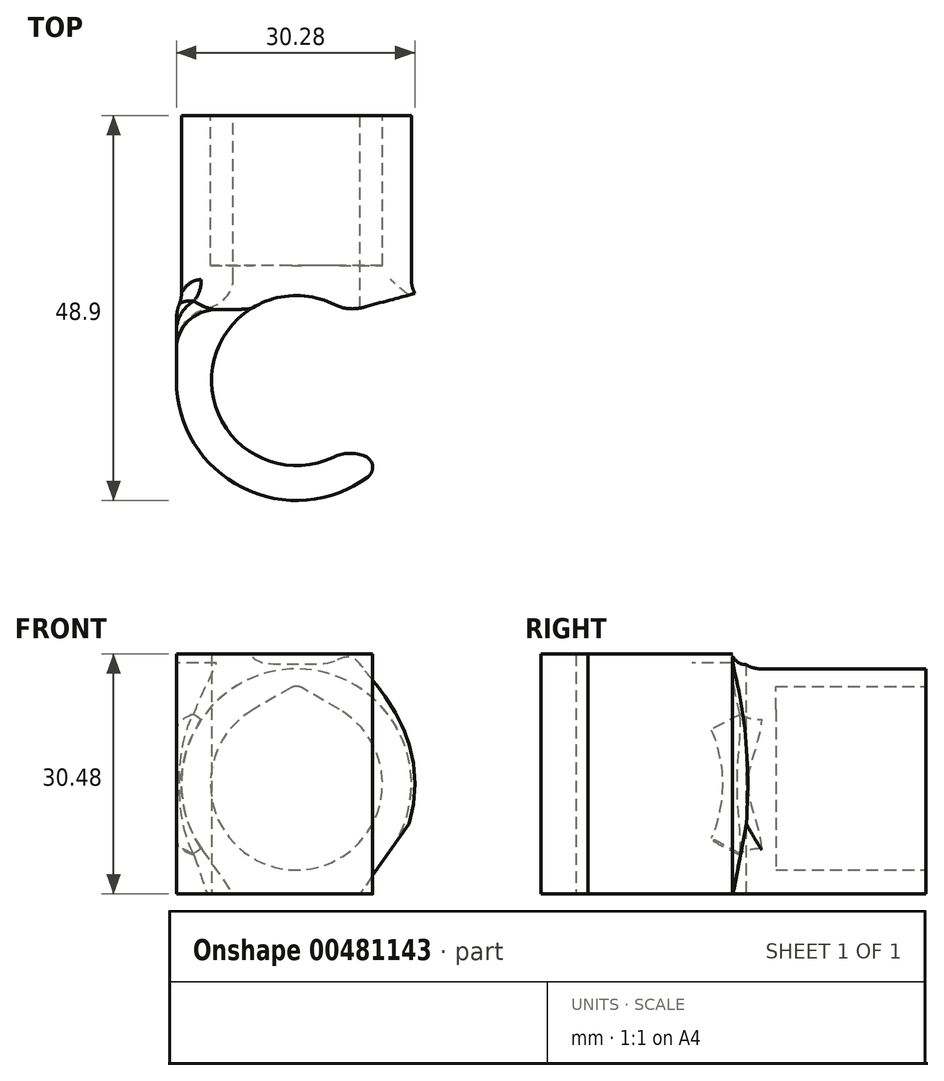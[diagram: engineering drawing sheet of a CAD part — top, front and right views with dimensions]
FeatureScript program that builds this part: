
annotation { "Feature Type Name" : "Feature", "Feature Type Description" : "" }
export const myFeature = defineFeature(function(context is Context, id is Id, definition is map)
    precondition{}
    {
        {
            var Q0;
            Q0=qCreatedBy(makeId("Top.planeOp"),FACE);
            var sketch = newSketch(context, id + "F0", { "sketchPlane" : qUnion([Q0])});
            skArc(sketch, "E0", {"start": v(4.84, 9.65) * mm, "mid": v(-10.8, 0.11) * mm, "end": v(4.64, -9.75) * mm});
            skArc(sketch, "E1", {"start": v(-15.24, 0) * mm, "mid": v(-6.85, -13.61) * mm, "end": v(9.08, -12.24) * mm});
            skLineSegment(sketch, "E2", {"start": v(-15.24, 0) * mm, "end": v(-15.24, 33.66) * mm});
            skLineSegment(sketch, "E3", {"start": v(15.24, 11.11) * mm, "end": v(15.24, 33.66) * mm});
            skLineSegment(sketch, "E4", {"start": v(15.24, 33.66) * mm, "end": v(-15.24, 33.66) * mm});
            skPoint(sketch, "E5.orphan", {"position": v(-10.8, 0) * mm});
            skPoint(sketch, "E6.start.orphan", {"position": v(10.8, 0) * mm});
            skLineSegment(sketch, "E7", {"start": v(8.43, 9.29) * mm, "end": v(15.24, 11.11) * mm});
            skPoint(sketch, "E8.orphan", {"position": v(15.24, 0) * mm});
            skPoint(sketch, "E9.visualSharp", {"position": v(6.35, 8.73) * mm});
            skArc(sketch, "E9.filletArc", {"start": v(4.84, 9.65) * mm, "mid": v(6.6, 9.14) * mm, "end": v(8.43, 9.29) * mm});
            skPoint(sketch, "E10.visualSharp", {"position": v(6.1, -8.9) * mm});
            skArc(sketch, "E10.filletArc", {"start": v(8.76, -9.64) * mm, "mid": v(6.69, -9.26) * mm, "end": v(4.64, -9.75) * mm});
            skArc(sketch, "E11", {"start": v(8.76, -9.64) * mm, "mid": v(9.68, -10.85) * mm, "end": v(9.08, -12.24) * mm});
            skSolve(sketch);
        }
        {
            var Q0;
            Q0 = qSketchRegion(id + "F0", true);
            extrude(context, id + "F1", {"entities" : qUnion([Q0]), "depth" : 30.48 * mm});
        }
        {
            var Q0;
            Q0=makeQuery(id+"F1.opExtrude","SWEPT_FACE",FACE,{"disambiguationData":[OSD([sQuery(id+"F0.wireOp",EDGE,"E4")])]});
            var sketch = newSketch(context, id + "F2", { "sketchPlane" : qUnion([Q0])});
            skArc(sketch, "E12", {"start": v(-5.46, 23.43) * mm, "mid": v(0, 3.05) * mm, "end": v(5.46, 23.43) * mm});
            skLineSegment(sketch, "E13", {"start": v(-5.46, 23.43) * mm, "end": v(-0.64, 26.22) * mm});
            skLineSegment(sketch, "E14", {"start": v(0.64, 26.22) * mm, "end": v(5.46, 23.43) * mm});
            skPoint(sketch, "E15.visualSharp", {"position": v(0, 26.58) * mm});
            skArc(sketch, "E15.filletArc", {"start": v(0.63, 26.22) * mm, "mid": v(0, 26.39) * mm, "end": v(-0.64, 26.22) * mm});
            skSolve(sketch);
        }
        {
            var Q0;
            Q0 = qSketchRegion(id + "F2", true);
            extrude(context, id + "F3", {"entities" : qUnion([Q0]), "operationType" : NewBodyOperationType.REMOVE, "oppositeDirection" : true, "depth" : 19.05 * mm});
        }
        {
            var Q0;
            Q0=makeQuery(id+"F1.opExtrude","SWEPT_FACE",FACE,{"disambiguationData":[OSD([sQuery(id+"F0.wireOp",EDGE,"E4")])]});
            var sketch = newSketch(context, id + "F4", { "sketchPlane" : qUnion([Q0])});
            skArc(sketch, "E16", {"start": v(11.96, 5.6) * mm, "mid": v(0, 28.58) * mm, "end": v(-11.96, 5.6) * mm});
            skLineSegment(sketch, "E17", {"start": v(-11.96, 5.6) * mm, "end": v(-8.05, 0) * mm});
            skLineSegment(sketch, "E18", {"start": v(11.96, 5.6) * mm, "end": v(8.05, 0) * mm});
            skLineSegment(sketch, "E19", {"start": v(-8.05, 0) * mm, "end": v(8.05, 0) * mm});
            skCircle(sketch, "E20", {"center": v(0, 13.97) * mm, "radius": 23.12 * mm});
            skSolve(sketch);
        }
        {
            var Q0;
            Q0 = qSketchRegion(id + "F4", true);
            extrude(context, id + "F5", {"entities" : qUnion([Q0]), "operationType" : NewBodyOperationType.REMOVE, "oppositeDirection" : true, "depth" : 24.64 * mm});
        }
        {
            var Q0;
            {var subQ0=sQuery(id+"F4.wireOp",EDGE,"E16");Q0=makeQuery(id+"F5.boolean.opBoolean","COPY",EDGE,{"disambiguationData":[TD([makeQuery(id+"F1.opExtrude","SWEPT_FACE",FACE,{"disambiguationData":[OSD([sQuery(id+"F0.wireOp",EDGE,"E0")])]})])],"derivedFrom":makeQuery(id+"F5.opExtrude","CAP_EDGE",EDGE,{"disambiguationData":[OSD([subQ0])],"isStart":false})});}
            fillet(context, id + "F6", {"entities" : qUnion([Q0]), "radius" : 3.8 * mm, "tangentPropagation" : true, "allowEdgeOverflow" : false});
        }
        {
            var Q0;
            {var subQ0=makeQuery(id+"F1.opExtrude","SWEPT_FACE",FACE,{"disambiguationData":[OSD([sQuery(id+"F0.wireOp",EDGE,"E2")])]});var subQ1=sQuery(id+"F4.wireOp",EDGE,"E16");Q0=makeQuery(id+"F6.opFillet","BLEND_EDGE",EDGE,{"blendedFrom":[makeQuery(id+"F5.boolean.opBoolean","COPY",EDGE,{"disambiguationData":[TD([makeQuery(id+"F1.opExtrude","SWEPT_FACE",FACE,{"disambiguationData":[OSD([sQuery(id+"F0.wireOp",EDGE,"E0")])]})])],"derivedFrom":makeQuery(id+"F5.opExtrude","CAP_EDGE",EDGE,{"disambiguationData":[OSD([subQ1])],"isStart":false})}),subQ0],"blendedInto":[subQ0]});}
            var Q1;
            {var subQ0=makeQuery(id+"F1.opExtrude","SWEPT_FACE",FACE,{"disambiguationData":[OSD([sQuery(id+"F0.wireOp",EDGE,"E2")])]});var subQ1=sQuery(id+"F4.wireOp",EDGE,"E18");var subQ2=sQuery(id+"F4.wireOp",EDGE,"E16");Q1=makeQuery(id+"F6.opFillet","BLEND_EDGE",EDGE,{"blendedFrom":[makeQuery(id+"F5.boolean.opBoolean","COPY",EDGE,{"disambiguationData":[TD([makeQuery(id+"F5.opExtrude","SWEPT_FACE",FACE,{"disambiguationData":[OSD([subQ1])]})])],"derivedFrom":makeQuery(id+"F5.opExtrude","CAP_EDGE",EDGE,{"disambiguationData":[OSD([subQ2])],"isStart":false})}),subQ0],"blendedInto":[subQ0]});}
            fillet(context, id + "F7", {"entities" : qUnion([Q0, Q1]), "radius" : 5.08 * mm, "tangentPropagation" : true, "allowEdgeOverflow" : false});
        }
    });
